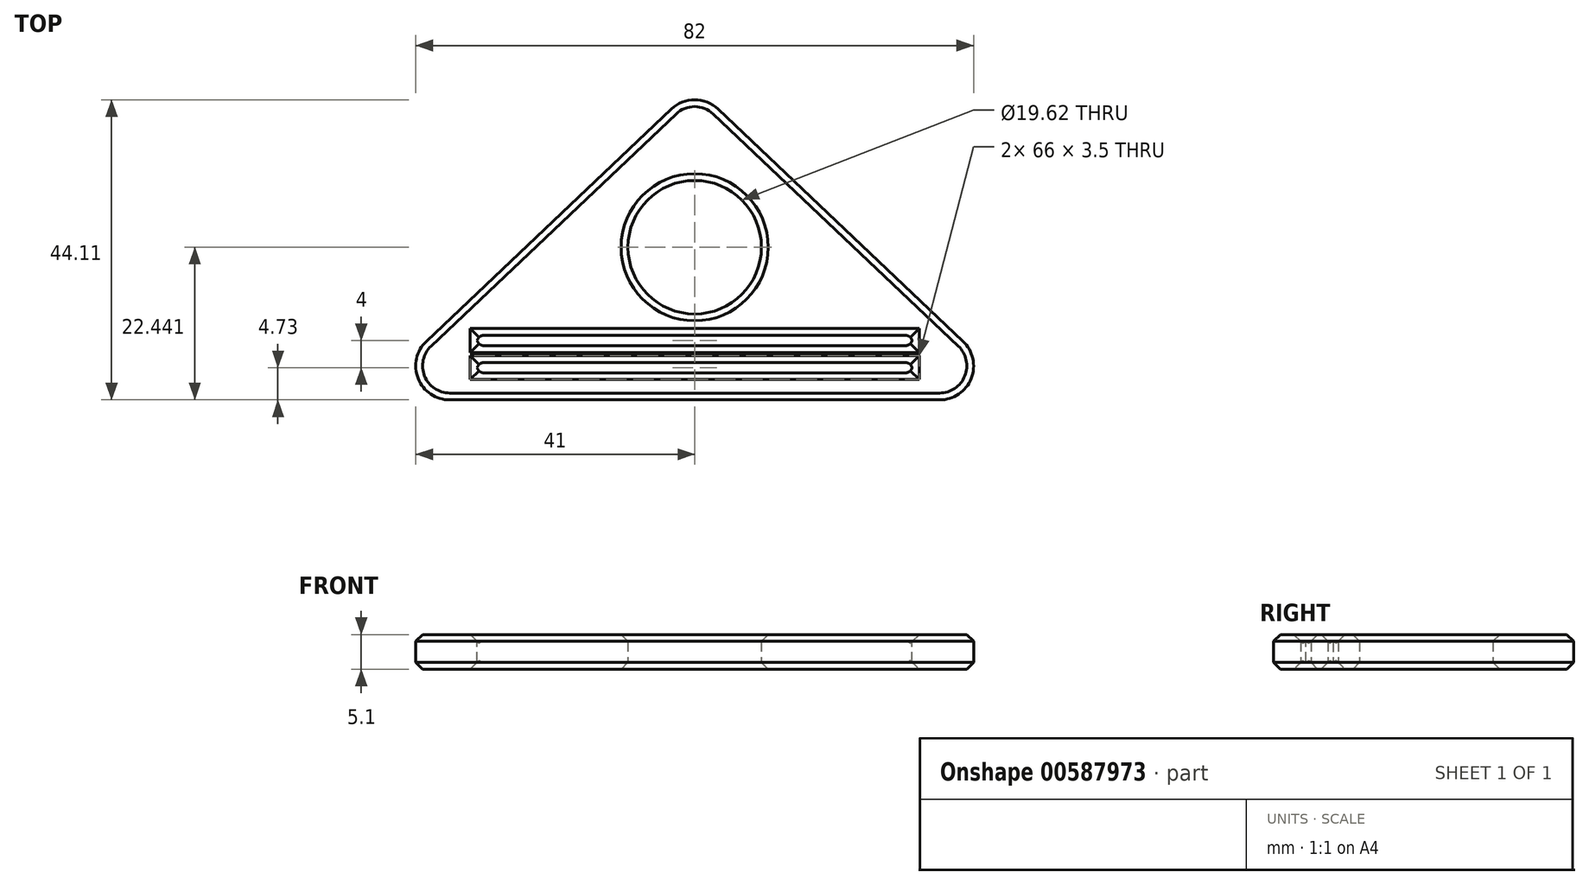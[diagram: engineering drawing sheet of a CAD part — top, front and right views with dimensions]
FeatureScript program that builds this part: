
annotation { "Feature Type Name" : "Feature", "Feature Type Description" : "" }
export const myFeature = defineFeature(function(context is Context, id is Id, definition is map)
    precondition{}
    {
        {
            var Q0;
            Q0=qCreatedBy(makeId("Top.planeOp"),FACE);
            var sketch = newSketch(context, id + "F0", { "sketchPlane" : qUnion([Q0])});
            skLineSegment(sketch, "E0.bottom", {"start": v(-32, 0) * mm, "end": v(32, 0) * mm});
            skLineSegment(sketch, "E0.top", {"start": v(-32, -1.5) * mm, "end": v(32, -1.5) * mm});
            skLineSegment(sketch, "E0.left", {"start": v(-32, 0) * mm, "end": v(-32, -1.5) * mm});
            skLineSegment(sketch, "E0.right", {"start": v(32, 0) * mm, "end": v(32, -1.5) * mm});
            skLineSegment(sketch, "E1.bottom", {"start": v(-32, 2.5) * mm, "end": v(32, 2.5) * mm});
            skLineSegment(sketch, "E1.top", {"start": v(-32, 4) * mm, "end": v(32, 4) * mm});
            skLineSegment(sketch, "E1.left", {"start": v(-32, 2.5) * mm, "end": v(-32, 4) * mm});
            skLineSegment(sketch, "E1.right", {"start": v(32, 2.5) * mm, "end": v(32, 4) * mm});
            skLineSegment(sketch, "E2", {"start": v(-48.55, -5.48) * mm, "end": v(48.55, -5.48) * mm});
            skLineSegment(sketch, "E3", {"start": v(0, -1.5) * mm, "end": v(0, -5.48) * mm, "construction": true});
            skLineSegment(sketch, "E4", {"start": v(-48.55, -5.48) * mm, "end": v(0, 40.52) * mm});
            skLineSegment(sketch, "E5", {"start": v(0, 40.52) * mm, "end": v(48.55, -5.48) * mm});
            skLineSegment(sketch, "E6", {"start": v(0, 40.52) * mm, "end": v(0, -5.48) * mm});
            skLineSegment(sketch, "E7", {"start": v(0, 4) * mm, "end": v(0, 40.52) * mm, "construction": true});
            skCircle(sketch, "E8", {"center": v(0, 16.96) * mm, "radius": 9.81 * mm});
            skSolve(sketch);
        }
        {
            var Q0;
            {var subQ7=sQuery(id+"F0.wireOp",EDGE,"E0.right");Q0=makeQuery(id+"F0.imprint","IMPRINT",FACE,{"disambiguationData":[TD([[makeQuery(id+"F0.imprint","IMPRINT",EDGE,{"derivedFrom":subQ7}),1.0]])]});}
            var Q1;
            {var subQ10=sQuery(id+"F0.wireOp",EDGE,"E0.left");Q1=makeQuery(id+"F0.imprint","IMPRINT",FACE,{"disambiguationData":[TD([[makeQuery(id+"F0.imprint","IMPRINT",EDGE,{"derivedFrom":subQ10}),-1.0]])]});}
            extrude(context, id + "F1", {"entities" : qUnion([Q0, Q1]), "depth" : 5.1 * mm, "offsetDistance" : 25 * mm});
        }
        {
            var Q0;
            Q0=makeQuery(id+"F1.opExtrude","SWEPT_EDGE",EDGE,{"disambiguationData":[OSD([sQuery(id+"F0.wireOp",EDGE,"E2"),sQuery(id+"F0.wireOp",EDGE,"E4")])]});
            var Q1;
            Q1=makeQuery(id+"F1.opExtrude","SWEPT_EDGE",EDGE,{"disambiguationData":[OSD([sQuery(id+"F0.wireOp",EDGE,"E2"),sQuery(id+"F0.wireOp",EDGE,"E5")])]});
            var Q2;
            Q2=makeQuery(id+"F1.opExtrude","SWEPT_EDGE",EDGE,{"disambiguationData":[OSD([sQuery(id+"F0.wireOp",EDGE,"E4"),sQuery(id+"F0.wireOp",EDGE,"E5"),sQuery(id+"F0.wireOp",EDGE,"E6")])]});
            fillet(context, id + "F2", {"entities" : qUnion([Q0, Q1, Q2]), "radius" : 5 * mm, "tangentPropagation" : true, "allowEdgeOverflow" : false});
        }
        {
            var Q0;
            Q0=makeQuery(id+"F1.opExtrude","CAP_FACE",FACE,{"disambiguationData":[OSD([sQuery(id+"F0.wireOp",EDGE,"E0.bottom"),sQuery(id+"F0.wireOp",EDGE,"E0.top"),sQuery(id+"F0.wireOp",EDGE,"E0.left"),sQuery(id+"F0.wireOp",EDGE,"E0.right"),sQuery(id+"F0.wireOp",EDGE,"E1.bottom"),sQuery(id+"F0.wireOp",EDGE,"E1.top"),sQuery(id+"F0.wireOp",EDGE,"E1.left"),sQuery(id+"F0.wireOp",EDGE,"E1.right"),sQuery(id+"F0.wireOp",EDGE,"E2"),sQuery(id+"F0.wireOp",EDGE,"E4"),sQuery(id+"F0.wireOp",EDGE,"E5"),sQuery(id+"F0.wireOp",EDGE,"E8")])],"isStart":false});
            var Q1;
            Q1=makeQuery(id+"F1.opExtrude","CAP_FACE",FACE,{"disambiguationData":[OSD([sQuery(id+"F0.wireOp",EDGE,"E0.bottom"),sQuery(id+"F0.wireOp",EDGE,"E0.top"),sQuery(id+"F0.wireOp",EDGE,"E0.left"),sQuery(id+"F0.wireOp",EDGE,"E0.right"),sQuery(id+"F0.wireOp",EDGE,"E1.bottom"),sQuery(id+"F0.wireOp",EDGE,"E1.top"),sQuery(id+"F0.wireOp",EDGE,"E1.left"),sQuery(id+"F0.wireOp",EDGE,"E1.right"),sQuery(id+"F0.wireOp",EDGE,"E2"),sQuery(id+"F0.wireOp",EDGE,"E4"),sQuery(id+"F0.wireOp",EDGE,"E5"),sQuery(id+"F0.wireOp",EDGE,"E8")])],"isStart":true});
            chamfer(context, id + "F3", {"entities" : qUnion([Q0, Q1]), "width" : 1 * mm, "tangentPropagation" : true});
        }
        {
            var Q0;
            Q0=makeQuery(id+"F1.opExtrude","SWEPT_EDGE",EDGE,{"disambiguationData":[OSD([sQuery(id+"F0.wireOp",EDGE,"E1.bottom"),sQuery(id+"F0.wireOp",EDGE,"E1.right")])]});
            var Q1;
            Q1=makeQuery(id+"F1.opExtrude","SWEPT_EDGE",EDGE,{"disambiguationData":[OSD([sQuery(id+"F0.wireOp",EDGE,"E0.bottom"),sQuery(id+"F0.wireOp",EDGE,"E0.right")])]});
            var Q2;
            Q2=makeQuery(id+"F1.opExtrude","SWEPT_EDGE",EDGE,{"disambiguationData":[OSD([sQuery(id+"F0.wireOp",EDGE,"E0.top"),sQuery(id+"F0.wireOp",EDGE,"E0.right")])]});
            var Q3;
            Q3=makeQuery(id+"F1.opExtrude","SWEPT_EDGE",EDGE,{"disambiguationData":[OSD([sQuery(id+"F0.wireOp",EDGE,"E1.top"),sQuery(id+"F0.wireOp",EDGE,"E1.right")])]});
            var Q4;
            Q4=makeQuery(id+"F1.opExtrude","SWEPT_EDGE",EDGE,{"disambiguationData":[OSD([sQuery(id+"F0.wireOp",EDGE,"E0.top"),sQuery(id+"F0.wireOp",EDGE,"E0.left")])]});
            var Q5;
            Q5=makeQuery(id+"F1.opExtrude","SWEPT_EDGE",EDGE,{"disambiguationData":[OSD([sQuery(id+"F0.wireOp",EDGE,"E1.bottom"),sQuery(id+"F0.wireOp",EDGE,"E1.left")])]});
            var Q6;
            Q6=makeQuery(id+"F1.opExtrude","SWEPT_EDGE",EDGE,{"disambiguationData":[OSD([sQuery(id+"F0.wireOp",EDGE,"E1.top"),sQuery(id+"F0.wireOp",EDGE,"E1.left")])]});
            var Q7;
            Q7=makeQuery(id+"F1.opExtrude","SWEPT_EDGE",EDGE,{"disambiguationData":[OSD([sQuery(id+"F0.wireOp",EDGE,"E0.bottom"),sQuery(id+"F0.wireOp",EDGE,"E0.left")])]});
            fillet(context, id + "F4", {"entities" : qUnion([Q0, Q1, Q2, Q3, Q4, Q5, Q6, Q7]), "radius" : 1 * mm, "tangentPropagation" : true, "allowEdgeOverflow" : false});
        }
    });
